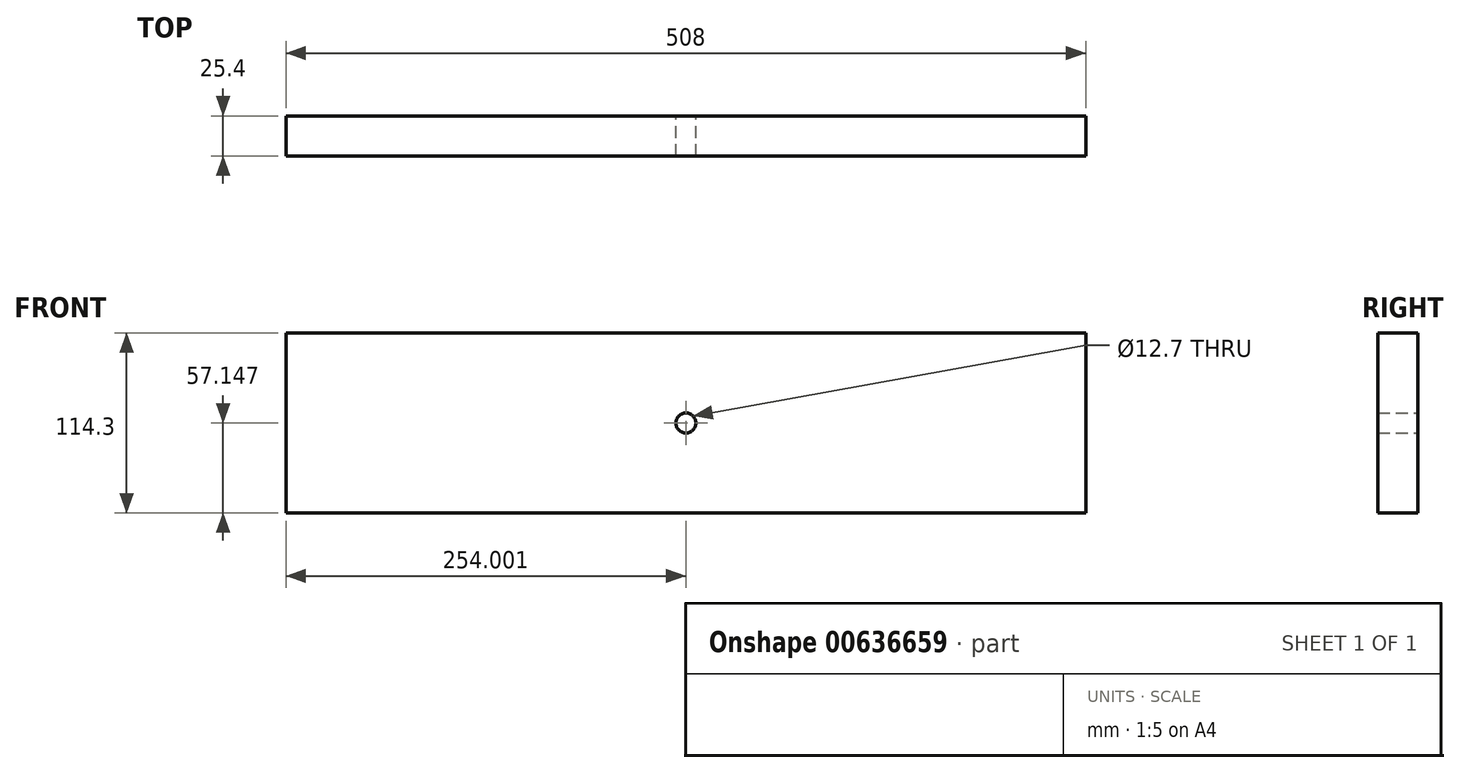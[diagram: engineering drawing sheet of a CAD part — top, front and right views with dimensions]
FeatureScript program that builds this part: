
annotation { "Feature Type Name" : "Feature", "Feature Type Description" : "" }
export const myFeature = defineFeature(function(context is Context, id is Id, definition is map)
    precondition{}
    {
        {
            var Q0;
            Q0=qCreatedBy(makeId("Front.planeOp"),FACE);
            var sketch = newSketch(context, id + "F0", { "sketchPlane" : qUnion([Q0])});
            skLineSegment(sketch, "E0.bottom", {"start": v(-242.33, -2.84) * mm, "end": v(265.67, -2.84) * mm});
            skLineSegment(sketch, "E0.top", {"start": v(-242.33, -117.14) * mm, "end": v(265.67, -117.14) * mm});
            skLineSegment(sketch, "E0.left", {"start": v(-242.33, -2.84) * mm, "end": v(-242.33, -117.14) * mm});
            skLineSegment(sketch, "E0.right", {"start": v(265.67, -2.84) * mm, "end": v(265.67, -117.14) * mm});
            skLineSegment(sketch, "E1", {"start": v(-216.93, -2.84) * mm, "end": v(-216.93, -117.14) * mm, "construction": true});
            skLineSegment(sketch, "E2", {"start": v(240.27, -2.84) * mm, "end": v(240.27, -117.14) * mm, "construction": true});
            skLineSegment(sketch, "E3", {"start": v(11.67, -2.84) * mm, "end": v(11.67, -117.14) * mm, "construction": true});
            skCircle(sketch, "E4", {"center": v(11.67, -60) * mm, "radius": 6.35 * mm});
            skSolve(sketch);
        }
        {
            var Q0;
            Q0 = qSketchRegion(id + "F0", true);
            extrude(context, id + "F1", {"entities" : qUnion([Q0]), "depth" : 25.4 * mm, "offsetDistance" : 25.4 * mm});
        }
    });
